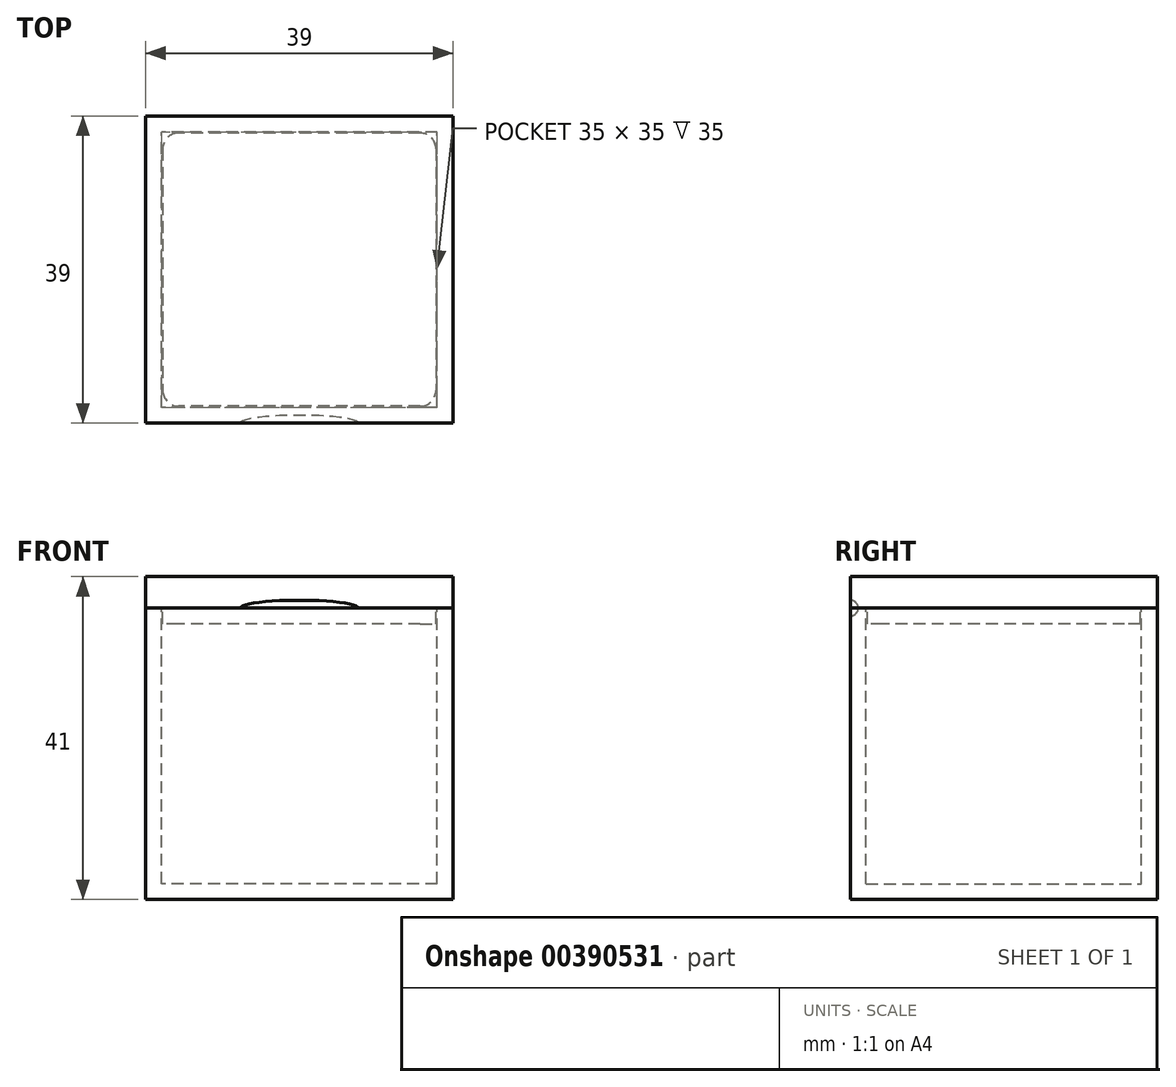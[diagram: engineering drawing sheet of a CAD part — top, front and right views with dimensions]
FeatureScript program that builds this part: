
annotation { "Feature Type Name" : "Feature", "Feature Type Description" : "" }
export const myFeature = defineFeature(function(context is Context, id is Id, definition is map)
    precondition{}
    {
        {
            var Q0;
            Q0=qCreatedBy(makeId("Top.planeOp"),FACE);
            var sketch = newSketch(context, id + "F0", { "sketchPlane" : qUnion([Q0])});
            skLineSegment(sketch, "E0.bottom", {"start": v(19.5, -19.5) * mm, "end": v(-19.5, -19.5) * mm});
            skLineSegment(sketch, "E0.top", {"start": v(19.5, 19.5) * mm, "end": v(-19.5, 19.5) * mm});
            skLineSegment(sketch, "E0.left", {"start": v(19.5, -19.5) * mm, "end": v(19.5, 19.5) * mm});
            skLineSegment(sketch, "E0.right", {"start": v(-19.5, -19.5) * mm, "end": v(-19.5, 19.5) * mm});
            skPoint(sketch, "E0.middle", {"position": v(0, 0) * mm});
            skSolve(sketch);
        }
        {
            var Q0;
            Q0=makeQuery(id+"F0.imprint","IMPRINT",FACE,{"disambiguationData":[TD([[makeQuery(id+"F0.imprint","IMPRINT",EDGE,{"derivedFrom":sQuery(id+"F0.wireOp",EDGE,"E0.bottom")}),-1.0]])]});
            extrude(context, id + "F1", {"entities" : qUnion([Q0]), "depth" : 37 * mm});
        }
        {
            var Q0;
            Q0=makeQuery(id+"F1.opExtrude","CAP_FACE",FACE,{"disambiguationData":[OSD([sQuery(id+"F0.wireOp",EDGE,"E0.bottom"),sQuery(id+"F0.wireOp",EDGE,"E0.top"),sQuery(id+"F0.wireOp",EDGE,"E0.left"),sQuery(id+"F0.wireOp",EDGE,"E0.right")])],"isStart":false});
            var sketch = newSketch(context, id + "F2", { "sketchPlane" : qUnion([Q0])});
            skLineSegment(sketch, "E1.bottom", {"start": v(17.5, -17.5) * mm, "end": v(-17.5, -17.5) * mm});
            skLineSegment(sketch, "E1.top", {"start": v(17.5, 17.5) * mm, "end": v(-17.5, 17.5) * mm});
            skLineSegment(sketch, "E1.left", {"start": v(17.5, -17.5) * mm, "end": v(17.5, 17.5) * mm});
            skLineSegment(sketch, "E1.right", {"start": v(-17.5, -17.5) * mm, "end": v(-17.5, 17.5) * mm});
            skPoint(sketch, "E1.middle", {"position": v(0, 0) * mm});
            skSolve(sketch);
        }
        {
            var Q0;
            Q0=makeQuery(id+"F2.imprint","IMPRINT",FACE,{"disambiguationData":[TD([[makeQuery(id+"F2.imprint","IMPRINT",EDGE,{"derivedFrom":sQuery(id+"F2.wireOp",EDGE,"E1.bottom")}),-1.0]])]});
            extrude(context, id + "F3", {"entities" : qUnion([Q0]), "operationType" : NewBodyOperationType.REMOVE, "oppositeDirection" : true, "depth" : 35 * mm});
        }
        {
            var Q0;
            Q0=makeQuery(id+"F1.opExtrude","CAP_FACE",FACE,{"disambiguationData":[OSD([sQuery(id+"F0.wireOp",EDGE,"E0.bottom"),sQuery(id+"F0.wireOp",EDGE,"E0.top"),sQuery(id+"F0.wireOp",EDGE,"E0.left"),sQuery(id+"F0.wireOp",EDGE,"E0.right")])],"isStart":false});
            var sketch = newSketch(context, id + "F4", { "sketchPlane" : qUnion([Q0])});
            skLineSegment(sketch, "E2.0", {"start": v(-19.5, -19.5) * mm, "end": v(-19.5, 19.5) * mm});
            skLineSegment(sketch, "E3.0", {"start": v(19.5, 19.5) * mm, "end": v(-19.5, 19.5) * mm});
            skLineSegment(sketch, "E4.0", {"start": v(19.5, -19.5) * mm, "end": v(19.5, 19.5) * mm});
            skLineSegment(sketch, "E5.0", {"start": v(19.5, -19.5) * mm, "end": v(-19.5, -19.5) * mm});
            skSolve(sketch);
        }
        {
            var Q0;
            Q0 = qSketchRegion(id + "F4", true);
            extrude(context, id + "F5", {"entities" : qUnion([Q0]), "depth" : 4 * mm});
        }
        {
            var Q0;
            Q0=makeQuery(id+"F5.opExtrude","CAP_FACE",FACE,{"disambiguationData":[OSD([sQuery(id+"F4.wireOp",EDGE,"E2.0"),sQuery(id+"F4.wireOp",EDGE,"E3.0"),sQuery(id+"F4.wireOp",EDGE,"E4.0"),sQuery(id+"F4.wireOp",EDGE,"E5.0")])],"isStart":true});
            var sketch = newSketch(context, id + "F6", { "sketchPlane" : qUnion([Q0])});
            skLineSegment(sketch, "E6.bottom", {"start": v(17.35, -17.35) * mm, "end": v(-17.35, -17.35) * mm});
            skLineSegment(sketch, "E6.top", {"start": v(17.35, 17.35) * mm, "end": v(-17.35, 17.35) * mm});
            skLineSegment(sketch, "E6.left", {"start": v(17.35, -17.35) * mm, "end": v(17.35, 17.35) * mm});
            skLineSegment(sketch, "E6.right", {"start": v(-17.35, -17.35) * mm, "end": v(-17.35, 17.35) * mm});
            skPoint(sketch, "E6.middle", {"position": v(0, 0) * mm});
            skSolve(sketch);
        }
        {
            var Q0;
            Q0 = qSketchRegion(id + "F6", true);
            extrude(context, id + "F7", {"entities" : qUnion([Q0]), "operationType" : NewBodyOperationType.ADD, "depth" : 2 * mm});
        }
        {
            var Q0;
            Q0=makeQuery(id+"F7.opExtrude","SWEPT_EDGE",EDGE,{"disambiguationData":[OSD([sQuery(id+"F6.wireOp",EDGE,"E6.top"),sQuery(id+"F6.wireOp",EDGE,"E6.right")])]});
            var Q1;
            Q1=makeQuery(id+"F7.opExtrude","SWEPT_EDGE",EDGE,{"disambiguationData":[OSD([sQuery(id+"F6.wireOp",EDGE,"E6.top"),sQuery(id+"F6.wireOp",EDGE,"E6.left")])]});
            var Q2;
            Q2=makeQuery(id+"F7.opExtrude","SWEPT_EDGE",EDGE,{"disambiguationData":[OSD([sQuery(id+"F6.wireOp",EDGE,"E6.bottom"),sQuery(id+"F6.wireOp",EDGE,"E6.right")])]});
            var Q3;
            Q3=makeQuery(id+"F7.opExtrude","SWEPT_EDGE",EDGE,{"disambiguationData":[OSD([sQuery(id+"F6.wireOp",EDGE,"E6.bottom"),sQuery(id+"F6.wireOp",EDGE,"E6.left")])]});
            fillet(context, id + "F8", {"entities" : qUnion([Q0, Q1, Q2, Q3]), "radius" : 2 * mm, "tangentPropagation" : true, "allowEdgeOverflow" : false});
        }
        {
            var Q0;
            Q0=makeQuery(id+"F1.opExtrude","CAP_FACE",FACE,{"disambiguationData":[OSD([sQuery(id+"F0.wireOp",EDGE,"E0.bottom"),sQuery(id+"F0.wireOp",EDGE,"E0.top"),sQuery(id+"F0.wireOp",EDGE,"E0.left"),sQuery(id+"F0.wireOp",EDGE,"E0.right")])],"isStart":false});
            var sketch = newSketch(context, id + "F9", { "sketchPlane" : qUnion([Q0])});
            skEllipse(sketch, "E7", {"center": v(0, -19.5) * mm, "majorRadius": 7.47 * mm, "minorRadius": 1 * mm, "majorAxis": v(1, 0)});
            skLineSegment(sketch, "E8", {"start": v(-17.5, -18.5) * mm, "end": v(24.62, -18.5) * mm, "construction": true});
            skSolve(sketch);
        }
        {
            var Q0;
            {var subQ0=sQuery(id+"F9.wireOp",EDGE,"E7");var subQ1=makeQuery(id+"F1.opExtrude","CAP_EDGE",EDGE,{"disambiguationData":[OSD([sQuery(id+"F0.wireOp",EDGE,"E0.bottom")])],"isStart":false});var subQ2=makeQuery(id+"F9.imprint","INTERSECT",VERTEX,{"disambiguationData":[OD(0.0)],"derivedFrom":[subQ1,subQ0]});Q0=makeQuery(id+"F9.imprint","IMPRINT",FACE,{"disambiguationData":[TD([[makeQuery(id+"F9.imprint","IMPRINT",EDGE,{"disambiguationData":[TD([[subQ2,-1.0]])],"derivedFrom":subQ0}),1.0]])]});}
            var Q1;
            Q1=makeQuery(id+"F1.opExtrude","CAP_EDGE",EDGE,{"disambiguationData":[OSD([sQuery(id+"F0.wireOp",EDGE,"E0.bottom")])],"isStart":false});
            revolve(context, id + "F10", {"entities" : qUnion([Q0]), "axis" : qUnion([Q1]), "revolveType" : RevolveType.FULL});
        }
        {
            var Q0;
            Q0=makeQuery(id+"F10.opRevolve","SWEPT_BODY",BODY,{"disambiguationData":[OSD([sQuery(id+"F0.wireOp",EDGE,"E0.bottom"),sQuery(id+"F9.wireOp",EDGE,"E7")])]});
            var Q1;
            Q1=makeQuery(id+"F5.opExtrude","SWEPT_BODY",BODY,{"disambiguationData":[OSD([sQuery(id+"F4.wireOp",EDGE,"E2.0"),sQuery(id+"F4.wireOp",EDGE,"E3.0"),sQuery(id+"F4.wireOp",EDGE,"E4.0"),sQuery(id+"F4.wireOp",EDGE,"E5.0")])]});
            var Q2;
            Q2=makeQuery(id+"F1.opExtrude","SWEPT_BODY",BODY,{"disambiguationData":[OSD([sQuery(id+"F0.wireOp",EDGE,"E0.bottom"),sQuery(id+"F0.wireOp",EDGE,"E0.top"),sQuery(id+"F0.wireOp",EDGE,"E0.left"),sQuery(id+"F0.wireOp",EDGE,"E0.right")])]});
            booleanBodies(context, id + "F11", {"operationType" : BooleanOperationType.SUBTRACTION, "tools" : qUnion([Q0]), "targets" : qUnion([Q1, Q2])});
        }
    });
